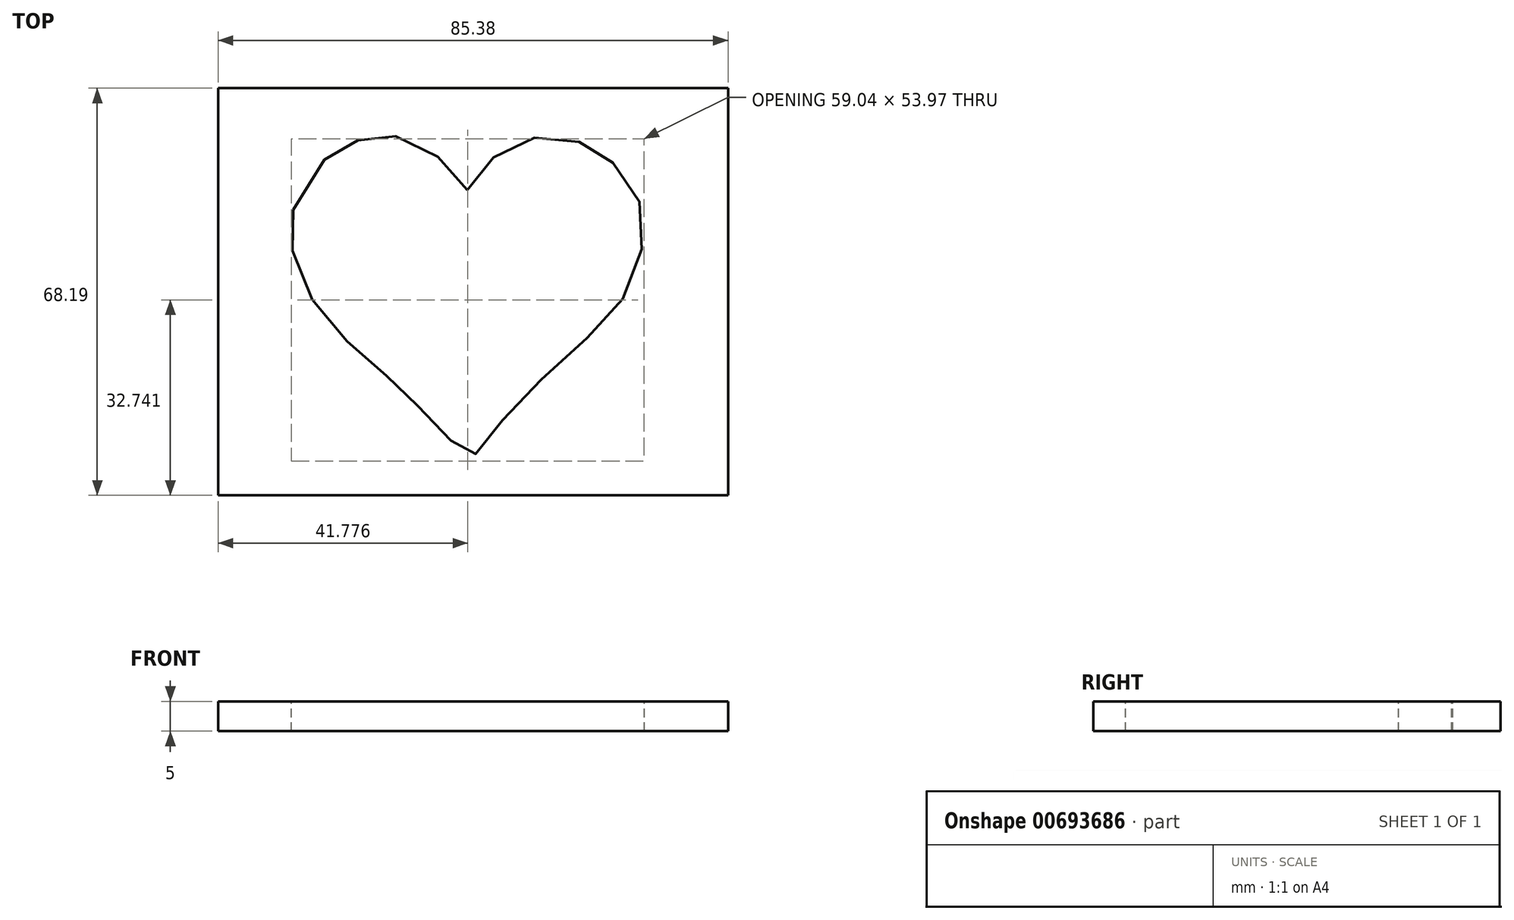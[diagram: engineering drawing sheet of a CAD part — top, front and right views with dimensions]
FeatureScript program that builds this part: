
annotation { "Feature Type Name" : "Feature", "Feature Type Description" : "" }
export const myFeature = defineFeature(function(context is Context, id is Id, definition is map)
    precondition{}
    {
        {
            var Q0;
            Q0=qCreatedBy(makeId("Top.planeOp"),FACE);
            var sketch = newSketch(context, id + "F0", { "sketchPlane" : qUnion([Q0])});
            skFitSpline(sketch, "E0", {"points": [v(29.44, 6.36) * mm, v(30.38, 8.23) * mm, v(33.65, 11.68) * mm, v(37.01, 13.74) * mm, v(41.31, 15.24) * mm, v(45.7, 15.24) * mm, v(49.07, 14.02) * mm, v(51.6, 12.62) * mm, v(54.4, 10.38) * mm, v(57.1, 7.1) * mm, v(58.9, 1.96) * mm, v(58.9, -2.34) * mm, v(57.4, -7.48) * mm, v(54.96, -12.71) * mm, v(51.5, -16.54) * mm, v(45.99, -21.6) * mm, v(40.47, -26.73) * mm, v(36.17, -31.31) * mm, v(32.9, -34.96) * mm, v(31.07, -37.41) * mm, v(29.45, -39.35) * mm, v(27.52, -36.85) * mm, v(24.25, -32.83) * mm, v(21.07, -29.75) * mm, v(18.27, -27.04) * mm, v(15.65, -24.51) * mm, v(11.63, -20.96) * mm, v(7.15, -16.94) * mm, v(3.5, -12.08) * mm, v(0.8, -6.28) * mm, v(0, -2.55) * mm, v(0, 0) * mm, v(0.98, 5.3) * mm, v(5.37, 11.29) * mm, v(7.05, 12.5) * mm, v(10.23, 14.28) * mm, v(13.22, 15.24) * mm, v(16.21, 15.24) * mm, v(19.3, 15.24) * mm, v(23.78, 12.4) * mm, v(27.43, 9.7) * mm, v(29.44, 6.36) * mm]});
            skText(sketch, "E1", { "text": "little mix", "fontName": "OpenSans-Bold.ttf"});
            skLineSegment(sketch, "E2.bottom", {"start": v(-12.28, 23.4) * mm, "end": v(73.1, 23.4) * mm});
            skLineSegment(sketch, "E2.top", {"start": v(-12.28, -44.78) * mm, "end": v(73.1, -44.78) * mm});
            skLineSegment(sketch, "E2.left", {"start": v(-12.28, 23.4) * mm, "end": v(-12.28, -44.78) * mm});
            skLineSegment(sketch, "E2.right", {"start": v(73.1, 23.4) * mm, "end": v(73.1, -44.78) * mm});
            const initialGuessF0  = {"E1": [0.01004, -0.00778, 1, 0, 0.00523]};
            skSetInitialGuess(sketch, initialGuessF0);
            skSolve(sketch);
        }
        {
            var Q0;
            Q0 = qSketchRegion(id + "F0", true);
            extrude(context, id + "F1", {"entities" : qUnion([Q0]), "oppositeDirection" : true, "depth" : 5 * mm, "offsetDistance" : 25.4 * mm});
        }
    });
